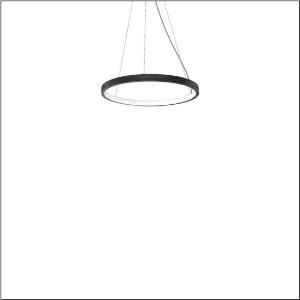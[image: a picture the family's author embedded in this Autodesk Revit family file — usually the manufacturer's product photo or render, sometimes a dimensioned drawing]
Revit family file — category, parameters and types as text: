
# Revit family: silica_21_ring-i_5pjbi1d1104a
name_source: partatom
category: Lighting Fixtures
units: mm (PartAtom-declared; Revit-internal decimal feet)

## family parameters
Cut with Voids When Loaded = No
Host = Face
Light Source = No
Part Type = Normal
Room Calculation Point = No
Round Connector Dimension = Use Diameter
Shared = No

## types (1)
- Silica 21 Ring-I (1 x LED, 3430 lm, 60 W, 3000K)
    Apparent Load = 60 VA
    CIE Flux Codes = 22 48 76 50 101
    Color Rendering = 80
    Color Temperature = 3000K
    Default Elevation = 1800 mm
    Description = Silica 21 Ring-I, suspended luminaire, of PMMA, frosted, light emission: inner ring side luminous distribution, primary light characteristic: symmetric, installation type: suspended mounting, LED, rated luminous flux: 3.430lm, luminous efficacy: 57lm/W, light colour: 830, colour temperature: 3000K, control gear: DALI 2, with terminal, 5-pole, mains connection: 230V, AC/DC, 0/50..60Hz, rated input power: 60W, housing, of extruded aluminium section, jet black (RAL 9005), diameter: 610mm, ceiling canopy, jet black (RAL 9005), protection rating (lamp compartment): IP40, insulation class (complete): insulation class I (protective earthing), certification: CE, impact resistance: IK02, permissible operating ambient temperature: 0..+35°C, packaging unit: 1 piece
    Height = 48 mm  [stored 0.15748 ft]
    Lamp = 1 x LED
    Lamp Light Flux = 3430 lm
    Lamp Power = 60 W
    Lamp count = 1
    Length = 610 mm
    Luminous efficacy = 57 lm/W
    Manufacturer = Siteco
    ModVariant = No
    Model = 5PJBI1D1104A
    Mounting Place = Ceiling
    Mounting Type = Pendant
    Number of Poles = 1
    OnlyDefault = Yes
    Power Factor = 1
    Product Name = Silica 21 Ring-I
    Product group = suspended luminaire
    ProductGroupID = 904
    Protection Class = Protection class I
    Protection Degree = IP 40
    RLX_Detail_Level = 1
    RLX_Emergency_Light_Flux = 0 lm
    RLX_Emergency_Type = 0
    RLX_Emergency_Type_DB = No
    RlxData = <blob elided: 12341 chars, md5=0cb1dbc2>
    Socket = socket
    Standby Power = 0 W
    System Light Flux = 3430 lm
    System Power = 60 W
    Type Comments = Product without accessories
    Type Image = l_1258361.jpg
    URL = http://relux.com
    VarID = ---
    Voltage = 0 V
    Weight = 0.00 kg
    Width = 0 mm  [stored 0 ft]

note: [stored X ft] marks values corroborated as IEEE doubles in the binary element streams (Revit-internal decimal feet)

## geometry (parser evidence)
native form markers: Sweep x11
no freeform markers — native parametric forms only
